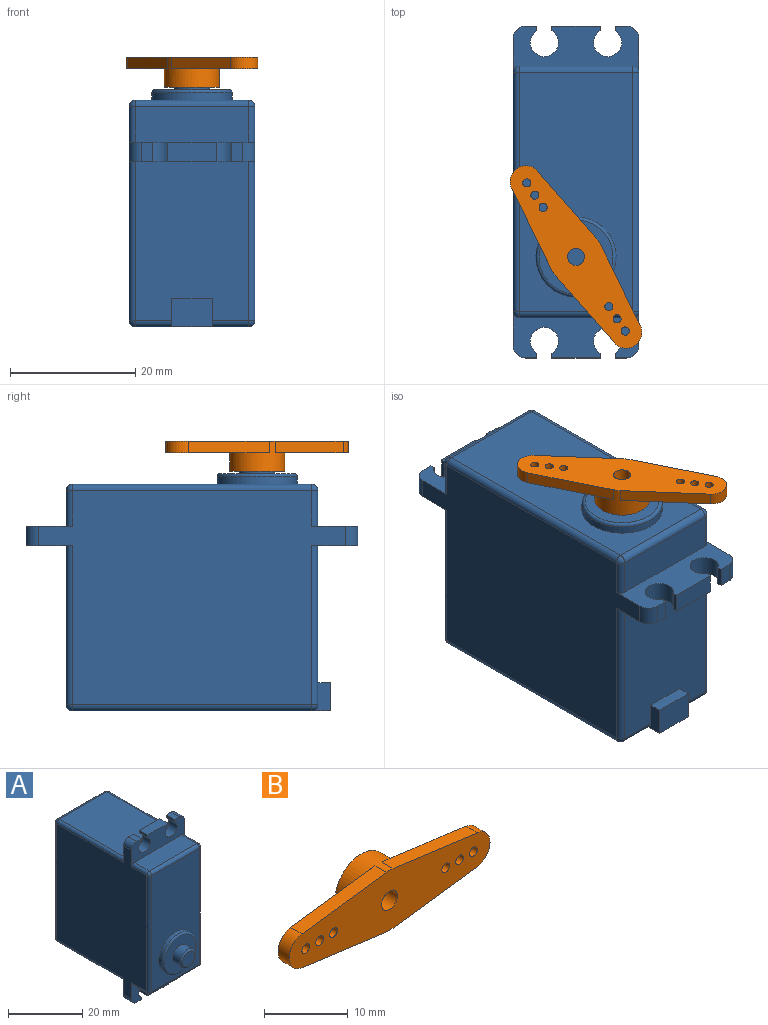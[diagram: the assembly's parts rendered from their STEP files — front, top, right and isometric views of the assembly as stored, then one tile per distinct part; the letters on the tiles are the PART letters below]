
ASSEMBLY  parts=2 mates=1
PART A: 69 faces, bbox 20.1x41.2x53 mm
  f0: plane 25.4x18.1mm, normal (0,0,1), area 459.7mm2, adj f33,f41,f44,f45
  f1: plane 25.4x18.1mm, normal (0,0,-1), area 437mm2, adj f22,f34,f35,f36,f38,f39,f47,f50
  f2: plane 18.1x5.7mm, normal (0,0,1), area 103.2mm2, adj f32,f53,f59,f62
  f3: plane 49x34.2mm, normal (-1,0,0), area 1339.9mm2, adj f21,f22,f32,f33,f38,f41,f42,f56
  f4: plane 18.1x5.7mm, normal (0,0,-1), area 103.2mm2, adj f21,f51,f55,f56
  f5: plane 49x34.2mm, normal (1,0,0), area 1339.9mm2, adj f21,f22,f32,f33,f44,f47,f48,f51
  f6: plane 38.2x18.1mm, normal (0,-1,0), area 562.7mm2, adj f8,f54,f55,f59,f60
  f7: plane 41.2x18.1mm, normal (0,1,0), area 710.9mm2, adj f35,f36,f37,f39,f42,f45,f48,f50
  f8: cylinder r=6.4mm len=12.8mm, axis (0,1,0), area 48.3mm2, adj f6,f64
  f9: plane 11.8x11.8mm, normal (0,-1,0), area 83.8mm2, adj f10,f64
  f10: cylinder r=2.85mm len=5.7mm, axis (0,1,0), area 50.1mm2, adj f9,f63
  f11: plane 4.7x4.7mm, normal (0,-1,0), area 17.3mm2, adj f63
  f12: cylinder r=2.25mm len=4.5mm, axis (0,1,0), area 36mm2, adj f13,f20,f21,f22
  f13: plane 3.1x0.73mm, normal (1,0,0), area 2.3mm2, adj f12,f14,f21,f22
  f14: plane 3.1x1.8mm, normal (0,0,-1), area 5.6mm2, adj f13,f21,f22,f67
  f15: plane 3.1x1.8mm, normal (0,0,-1), area 5.6mm2, adj f16,f21,f22,f68
  f16: plane 3.1x0.73mm, normal (-1,0,0), area 2.3mm2, adj f15,f17,f21,f22
  f17: cylinder r=2.25mm len=4.5mm, axis (0,1,0), area 36mm2, adj f16,f18,f21,f22
  f18: plane 3.1x0.73mm, normal (1,0,0), area 2.3mm2, adj f17,f19,f21,f22
  f19: plane 7.7x3.1mm, normal (0,0,-1), area 23.9mm2, adj f18,f20,f21,f22
  f20: plane 3.1x0.73mm, normal (-1,0,0), area 2.3mm2, adj f12,f19,f21,f22
  f21: plane 20.1x7.4mm, normal (0,-1,0), area 93.2mm2, adj f3,f4,f5,f12,f13,f14,f15,f16
  f22: plane 20.1x7.4mm, normal (0,1,0), area 93.2mm2, adj f1,f3,f5,f12,f13,f14,f15,f16
  f23: plane 3.1x0.73mm, normal (-1,0,0), area 2.3mm2, adj f24,f31,f32,f33
  f24: plane 7.7x3.1mm, normal (0,0,1), area 23.9mm2, adj f23,f25,f32,f33
  f25: plane 3.1x0.73mm, normal (1,0,0), area 2.3mm2, adj f24,f26,f32,f33
  f26: cylinder r=2.25mm len=4.5mm, axis (0,1,0), area 36mm2, adj f25,f27,f32,f33
  f27: plane 3.1x0.73mm, normal (-1,0,0), area 2.3mm2, adj f26,f28,f32,f33
  f28: plane 3.1x1.8mm, normal (0,0,1), area 5.6mm2, adj f27,f32,f33,f65
  f29: plane 3.1x1.8mm, normal (0,0,1), area 5.6mm2, adj f30,f32,f33,f66
  f30: plane 3.1x0.73mm, normal (1,0,0), area 2.3mm2, adj f29,f31,f32,f33
  f31: cylinder r=2.25mm len=4.5mm, axis (0,1,0), area 36mm2, adj f23,f30,f32,f33
  f32: plane 20.1x7.4mm, normal (0,-1,0), area 93.2mm2, adj f2,f3,f5,f23,f24,f25,f26,f27
  f33: plane 20.1x7.4mm, normal (0,1,0), area 93.2mm2, adj f0,f3,f5,f23,f24,f25,f26,f27
  f34: plane 6.5x2mm, normal (0,-1,0), area 13mm2, adj f1,f35,f36,f37
  f35: plane 4.5x3mm, normal (-1,0,0), area 9.2mm2, adj f1,f7,f34,f37,f39
  f36: plane 4.5x3mm, normal (1,0,0), area 9.2mm2, adj f1,f7,f34,f37,f50
  f37: plane 6.5x4.5mm, normal (0,0,-1), area 29.2mm2, adj f7,f34,f35,f36
  f38: cylinder r=1mm len=25.4mm, axis (0,1,0), area 39.9mm2, adj f1,f3,f22,f40
  f39: cylinder r=1mm len=5.8mm, axis (1,0,0), area 9.1mm2, adj f1,f7,f35,f40
  f40: sphere r=1mm, area 1.6mm2, adj f38,f39,f42
  f41: cylinder r=1mm len=25.4mm, axis (0,-1,0), area 39.9mm2, adj f0,f3,f33,f43
  f42: cylinder r=1mm len=38.2mm, axis (0,0,-1), area 60mm2, adj f3,f7,f40,f43
  f43: sphere r=1mm, area 1.6mm2, adj f41,f42,f45
  f44: cylinder r=1mm len=25.4mm, axis (0,1,0), area 39.9mm2, adj f0,f5,f33,f46
  f45: cylinder r=1mm len=18.1mm, axis (-1,0,0), area 28.4mm2, adj f0,f7,f43,f46
  f46: sphere r=1mm, area 1.6mm2, adj f44,f45,f48
  f47: cylinder r=1mm len=25.4mm, axis (0,-1,0), area 39.9mm2, adj f1,f5,f22,f49
  f48: cylinder r=1mm len=38.2mm, axis (0,0,1), area 60mm2, adj f5,f7,f46,f49
  f49: sphere r=1mm, area 1.6mm2, adj f47,f48,f50
  f50: cylinder r=1mm len=5.8mm, axis (1,0,0), area 9.1mm2, adj f1,f7,f36,f49
  f51: cylinder r=1mm len=5.7mm, axis (0,-1,0), area 9mm2, adj f4,f5,f21,f52
  f52: sphere r=1mm, area 1.6mm2, adj f51,f54,f55
  f53: cylinder r=1mm len=5.7mm, axis (0,1,0), area 9mm2, adj f2,f5,f32,f57
  f54: cylinder r=1mm len=38.2mm, axis (0,0,-1), area 60mm2, adj f5,f6,f52,f57
  f55: cylinder r=1mm len=18.1mm, axis (-1,0,0), area 28.4mm2, adj f4,f6,f52,f58
  f56: cylinder r=1mm len=5.7mm, axis (0,1,0), area 9mm2, adj f3,f4,f21,f58
  f57: sphere r=1mm, area 1.6mm2, adj f53,f54,f59
  f58: sphere r=1mm, area 1.6mm2, adj f55,f56,f60
  f59: cylinder r=1mm len=18.1mm, axis (1,0,0), area 28.4mm2, adj f2,f6,f57,f61
  f60: cylinder r=1mm len=38.2mm, axis (0,0,1), area 60mm2, adj f3,f6,f58,f61
  f61: sphere r=1mm, area 1.6mm2, adj f59,f60,f62
  f62: cylinder r=1mm len=5.7mm, axis (0,-1,0), area 9mm2, adj f2,f3,f32,f61
  f63: torus R=2.35mm, axis (0,-1,0), area 13.2mm2, adj f10,f11
  f64: torus R=5.9mm, axis (0,-1,0), area 30.7mm2, adj f8,f9
  f65: cylinder r=2mm len=3.1mm, axis (0,1,0), area 9.7mm2, adj f5,f28,f32,f33
  f66: cylinder r=2mm len=3.1mm, axis (0,-1,0), area 9.7mm2, adj f3,f29,f32,f33
  f67: cylinder r=2mm len=3.1mm, axis (0,1,0), area 9.7mm2, adj f3,f14,f21,f22
  f68: cylinder r=2mm len=3.1mm, axis (0,-1,0), area 9.7mm2, adj f5,f15,f21,f22
PART B: 20 faces, bbox 34x4.8x8.8 mm
  f0: plane 34x8.8mm, normal (0,-1,0), area 207.8mm2, adj f2,f4,f6,f7,f8,f9,f10,f13
  f1: cylinder r=2.6mm len=5.2mm, axis (0,1,0), area 47.4mm2, adj f3,f12
  f2: cylinder r=4.4mm len=8.8mm, axis (0,1,0), area 84.6mm2, adj f0,f3,f5,f6,f7,f8,f10,f11
  f3: plane 8.8x8.8mm, normal (0,1,0), area 39.6mm2, adj f1,f2
  f4: cylinder r=2.5mm len=4.96mm, axis (0,-1,0), area 13.7mm2, adj f0,f5,f6,f7
  f5: plane 16.42x8.72mm, normal (0,1,0), area 76.3mm2, adj f2,f4,f6,f7,f16,f17,f18
  f6: plane 14.25x1.9mm, normal (-0.13,0,0.99), area 27.3mm2, adj f0,f2,f4,f5
  f7: plane 14.25x1.9mm, normal (-0.13,0,-0.99), area 27.3mm2, adj f0,f2,f4,f5
  f8: plane 14.25x1.9mm, normal (0.13,0,0.99), area 27.3mm2, adj f0,f2,f9,f11
  f9: cylinder r=2.5mm len=4.96mm, axis (0,-1,0), area 13.7mm2, adj f0,f8,f10,f11
  f10: plane 14.25x1.9mm, normal (0.13,0,-0.99), area 27.3mm2, adj f0,f2,f9,f11
  f11: plane 16.42x8.72mm, normal (0,1,0), area 76.3mm2, adj f2,f8,f9,f10,f13,f14,f15
  f12: plane 5.2x5.2mm, normal (0,1,0), area 15.5mm2, adj f1,f19
  f13: cylinder r=0.65mm len=1.9mm, axis (0,-1,0), area 7.8mm2, adj f0,f11
  f14: cylinder r=0.65mm len=1.9mm, axis (0,-1,0), area 7.8mm2, adj f0,f11
  f15: cylinder r=0.65mm len=1.9mm, axis (0,-1,0), area 7.8mm2, adj f0,f11
  f16: cylinder r=0.65mm len=1.9mm, axis (0,-1,0), area 7.8mm2, adj f0,f5
  f17: cylinder r=0.65mm len=1.9mm, axis (0,-1,0), area 7.8mm2, adj f0,f5
  f18: cylinder r=0.65mm len=1.9mm, axis (0,-1,0), area 7.8mm2, adj f0,f5
  f19: cylinder r=1.35mm len=2.7mm, axis (0,-1,0), area 16.1mm2, adj f0,f12
PLACE A rot(axis=(-1,0,0),90deg) t=(0,0,-26.9)mm
PLACE B rot(axis=(-0.8,0.43,-0.43),102.9deg) t=(0,0,11.4)mm
MATE revolute A.f10 <-> B.f1  axis (0,0,1) through (0,0,14.3)mm
